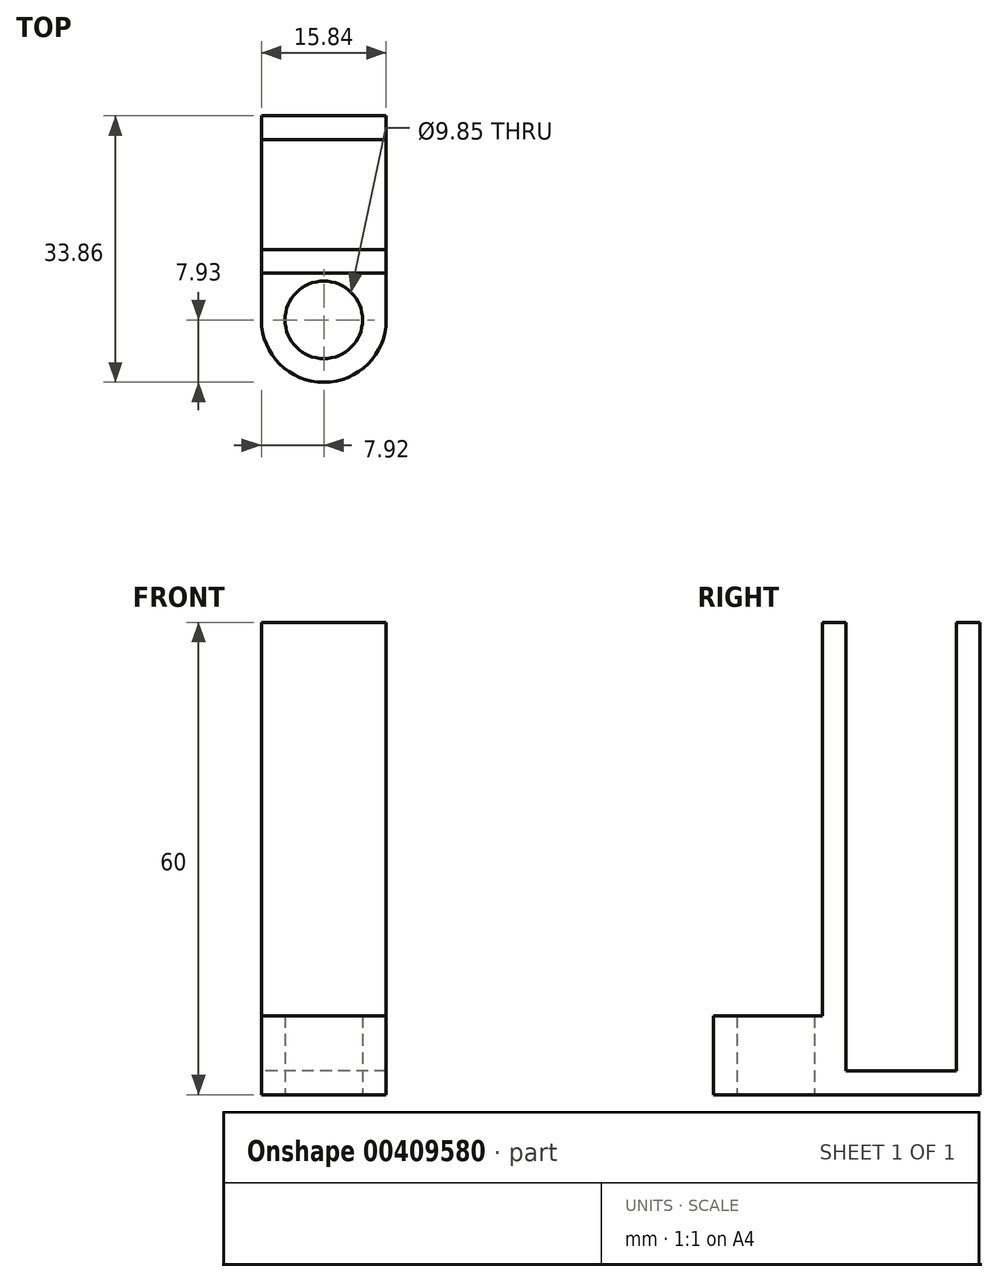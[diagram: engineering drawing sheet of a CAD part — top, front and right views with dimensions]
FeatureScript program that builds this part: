
annotation { "Feature Type Name" : "Feature", "Feature Type Description" : "" }
export const myFeature = defineFeature(function(context is Context, id is Id, definition is map)
    precondition{}
    {
        {
            var Q0;
            Q0=qCreatedBy(makeId("Top.planeOp"),FACE);
            var sketch = newSketch(context, id + "F0", { "sketchPlane" : qUnion([Q0])});
            skCircle(sketch, "E0", {"center": v(0, 0) * mm, "radius": 4.92 * mm});
            skArc(sketch, "E1.0", {"start": v(-7.92, 0) * mm, "mid": v(0, -7.92) * mm, "end": v(7.92, 0) * mm});
            skLineSegment(sketch, "E2.top", {"start": v(-7.93, 25.93) * mm, "end": v(7.92, 25.93) * mm});
            skLineSegment(sketch, "E2.left", {"start": v(-7.92, 0) * mm, "end": v(-7.92, 25.93) * mm});
            skLineSegment(sketch, "E2.right", {"start": v(7.92, 0) * mm, "end": v(7.92, 25.93) * mm});
            skLineSegment(sketch, "E3", {"start": v(-7.93, 22.93) * mm, "end": v(7.92, 22.93) * mm});
            skLineSegment(sketch, "E4", {"start": v(-7.93, 5.92) * mm, "end": v(7.92, 5.92) * mm});
            skPoint(sketch, "E5.end.orphan", {"position": v(7.92, 4.92) * mm});
            skLineSegment(sketch, "E6", {"start": v(-7.93, 8.92) * mm, "end": v(7.92, 8.92) * mm});
            skSolve(sketch);
        }
        {
            var Q0;
            Q0 = qSketchRegion(id + "F0", true);
            extrude(context, id + "F1", {"entities" : qUnion([Q0]), "depth" : 3 * mm});
        }
        {
            var Q0;
            {var subQ0=sQuery(id+"F0.wireOp",EDGE,"E4");Q0=makeQuery(id+"F0.imprint","IMPRINT",FACE,{"disambiguationData":[TD([[makeQuery(id+"F0.imprint","IMPRINT",EDGE,{"derivedFrom":subQ0}),1.0]])]});}
            var Q1;
            {var subQ0=sQuery(id+"F0.wireOp",EDGE,"E2.top");Q1=makeQuery(id+"F0.imprint","IMPRINT",FACE,{"disambiguationData":[TD([[makeQuery(id+"F0.imprint","IMPRINT",EDGE,{"derivedFrom":subQ0}),-1.0]])]});}
            extrude(context, id + "F2", {"entities" : qUnion([Q0, Q1]), "operationType" : NewBodyOperationType.ADD, "depth" : 60 * mm});
        }
        {
            var Q0;
            Q0=makeQuery(id+"F0.imprint","IMPRINT",FACE,{"disambiguationData":[TD([[makeQuery(id+"F0.imprint","IMPRINT",EDGE,{"derivedFrom":sQuery(id+"F0.wireOp",EDGE,"E0")}),-1.0]])]});
            extrude(context, id + "F3", {"entities" : qUnion([Q0]), "operationType" : NewBodyOperationType.ADD, "depth" : 10 * mm});
        }
    });
